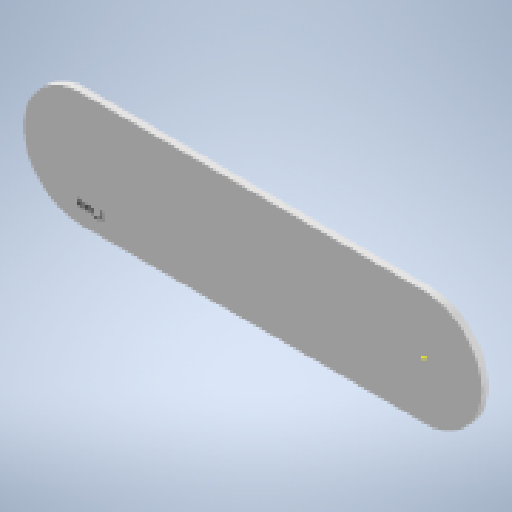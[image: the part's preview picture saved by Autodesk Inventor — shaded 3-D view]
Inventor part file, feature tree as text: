
AUTODESK INVENTOR PART (.ipt)
format: ipt  version: 2023 (Build 270158000, 158)  size: 139,264 bytes
history: native  units: mm
features: sketch x3, extrude x2, other x1
ambient origin geometry x8: Origin, YZ Plane, XZ Plane, XY Plane, X Axis, Y Axis, Z Axis, Center Point
bodies: Body1 (feature_tree)
feature tree (6):
  other  "實體1"
  extrude  "擠出1"  Depth=50.0mm
  sketch  "草圖2"
  extrude  "擠出2"  Depth=250.0mm
  sketch  "草圖1"
  sketch  "草圖3"
